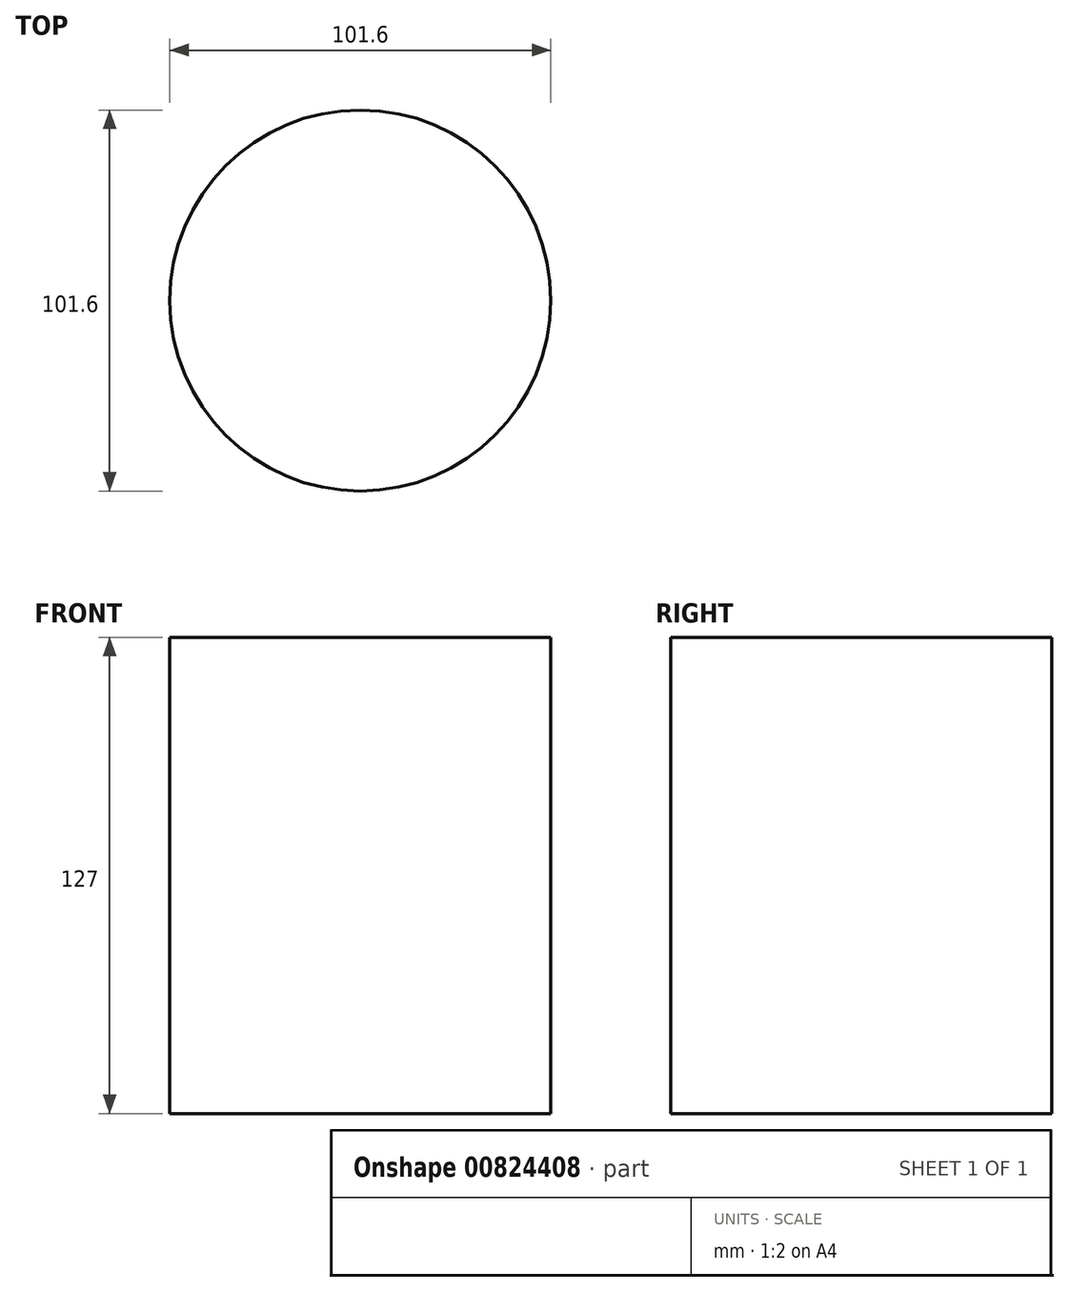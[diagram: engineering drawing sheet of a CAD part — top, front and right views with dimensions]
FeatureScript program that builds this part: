
annotation { "Feature Type Name" : "Feature", "Feature Type Description" : "" }
export const myFeature = defineFeature(function(context is Context, id is Id, definition is map)
    precondition{}
    {
        {
            var Q0;
            Q0=qCreatedBy(makeId("Top.planeOp"),FACE);
            var sketch = newSketch(context, id + "F0", { "sketchPlane" : qUnion([Q0])});
            skCircle(sketch, "E0", {"center": v(0, 0) * mm, "radius": 50.8 * mm});
            skSolve(sketch);
        }
        {
            var Q0;
            Q0=makeQuery(id+"F0.imprint","IMPRINT",FACE,{"disambiguationData":[TD([[makeQuery(id+"F0.imprint","IMPRINT",EDGE,{"derivedFrom":sQuery(id+"F0.wireOp",EDGE,"E0")}),1.0]])]});
            extrude(context, id + "F1", {"entities" : qUnion([Q0]), "depth" : 127 * mm, "offsetDistance" : 25.4 * mm});
        }
    });
